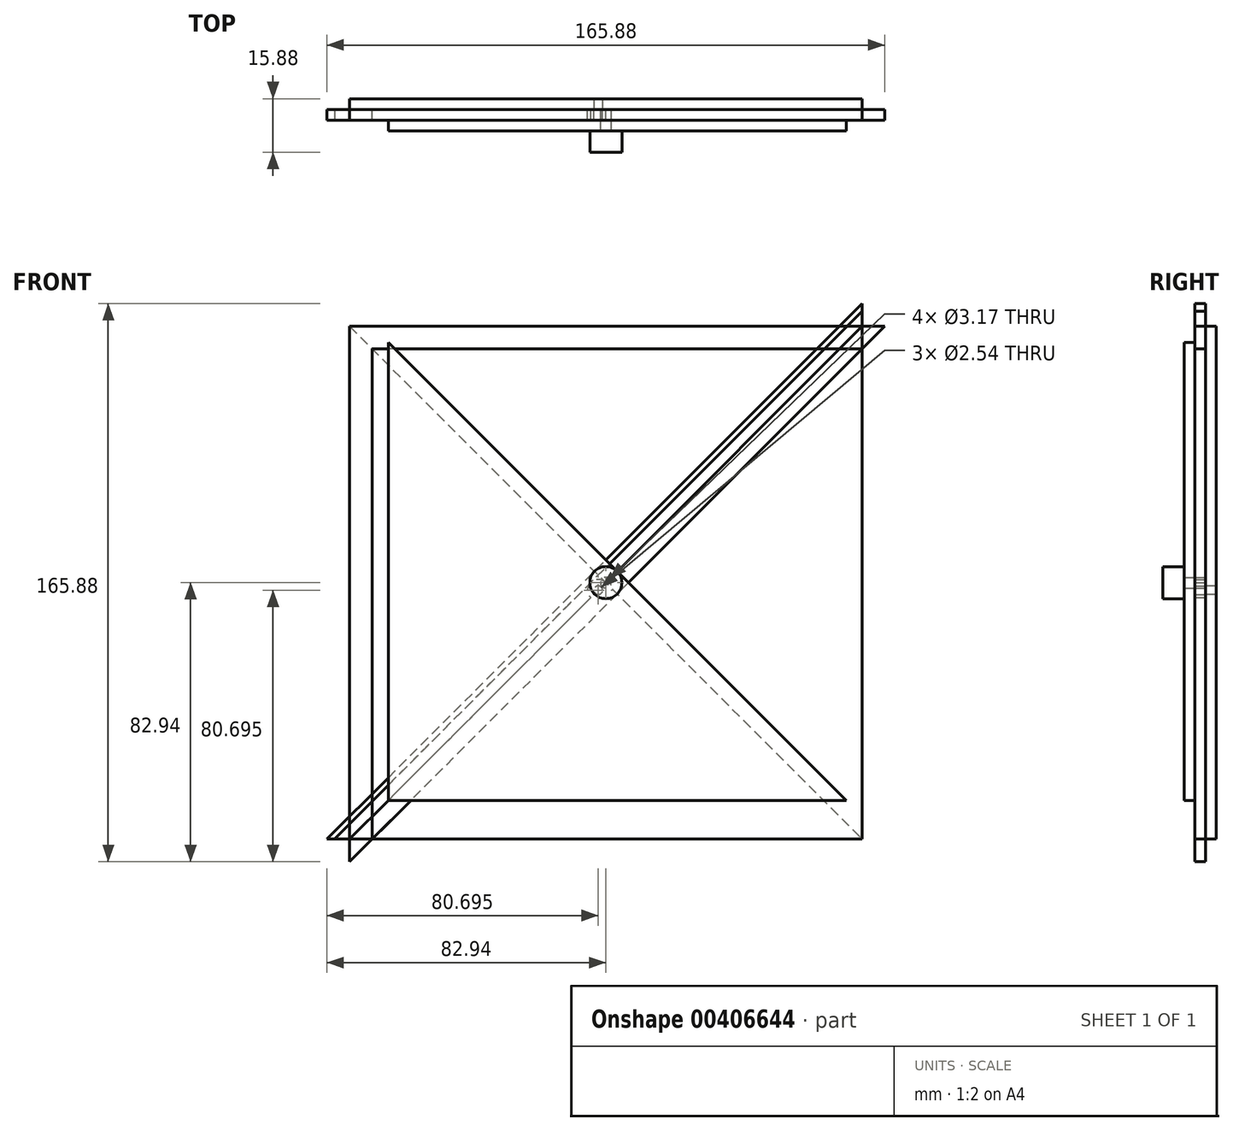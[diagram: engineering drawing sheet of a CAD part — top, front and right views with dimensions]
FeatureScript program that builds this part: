
annotation { "Feature Type Name" : "Feature", "Feature Type Description" : "" }
export const myFeature = defineFeature(function(context is Context, id is Id, definition is map)
    precondition{}
    {
        {
            var Q0;
            Q0=qCreatedBy(makeId("Front.planeOp"),FACE);
            var sketch = newSketch(context, id + "F0", { "sketchPlane" : qUnion([Q0])});
            skLineSegment(sketch, "E0.bottom", {"start": v(76.2, 76.2) * mm, "end": v(-76.2, 76.2) * mm});
            skLineSegment(sketch, "E0.top", {"start": v(76.2, -76.2) * mm, "end": v(-76.2, -76.2) * mm});
            skLineSegment(sketch, "E0.left", {"start": v(76.2, 76.2) * mm, "end": v(76.2, -76.2) * mm});
            skLineSegment(sketch, "E0.right", {"start": v(-76.2, 76.2) * mm, "end": v(-76.2, -76.2) * mm});
            skPoint(sketch, "E0.middle", {"position": v(0, 0) * mm});
            skLineSegment(sketch, "E1", {"start": v(-76.2, -76.2) * mm, "end": v(76.2, 76.2) * mm});
            skLineSegment(sketch, "E2", {"start": v(-76.2, 76.2) * mm, "end": v(76.2, -76.2) * mm});
            skCircle(sketch, "E3", {"center": v(-2.25, -2.25) * mm, "radius": 3.18 * mm});
            skSolve(sketch);
        }
        {
            var Q0;
            Q0=qCreatedBy(makeId("Front.planeOp"),FACE);
            var sketch = newSketch(context, id + "F1", { "sketchPlane" : qUnion([Q0])});
            skArc(sketch, "E4.0", {"start": v(0, 0) * mm, "mid": v(-4.5, 0) * mm, "end": v(-4.5, -4.5) * mm});
            skLineSegment(sketch, "E4.1", {"start": v(-76.2, -76.2) * mm, "end": v(-4.5, -4.5) * mm});
            skLineSegment(sketch, "E4.2", {"start": v(76.2, 76.2) * mm, "end": v(76.2, -76.2) * mm});
            skLineSegment(sketch, "E4.3", {"start": v(76.2, -76.2) * mm, "end": v(-76.2, -76.2) * mm});
            skLineSegment(sketch, "E5.trimOffspring", {"start": v(0, 0) * mm, "end": v(76.2, 76.2) * mm});
            skCircle(sketch, "E6", {"center": v(-2.25, -2.25) * mm, "radius": 1.27 * mm});
            skSolve(sketch);
        }
        {
            var Q0;
            Q0=qSketchRegion(id+"F1",true);
            extrude(context, id + "F2", {"entities" : qUnion([Q0]), "depth" : 3.17 * mm});
        }
        {
            var Q0;
            Q0=qCreatedBy(makeId("Front.planeOp"),FACE);
            var sketch = newSketch(context, id + "F3", { "sketchPlane" : qUnion([Q0])});
            skLineSegment(sketch, "E7.0", {"start": v(-76.2, 76.2) * mm, "end": v(76.2, -76.2) * mm});
            skLineSegment(sketch, "E7.1", {"start": v(-76.2, 76.2) * mm, "end": v(-76.2, -76.2) * mm});
            skLineSegment(sketch, "E7.2", {"start": v(76.2, -76.2) * mm, "end": v(-76.2, -76.2) * mm});
            skCircle(sketch, "E7.3", {"center": v(-2.25, -2.25) * mm, "radius": 1.27 * mm});
            skSolve(sketch);
        }
        {
            var Q0;
            Q0=qSketchRegion(id+"F3",true);
            extrude(context, id + "F4", {"entities" : qUnion([Q0]), "oppositeDirection" : true, "depth" : 3.17 * mm});
        }
        {
            var Q0;
            Q0=qCreatedBy(makeId("Right.planeOp"),FACE);
            var Q1;
            Q1=sQuery(id+"F0.wireOp",VERTEX,"E3.center");
            cPlane(context, id + "F5", {"entities" : qUnion([Q0, Q1]), "cplaneType" : CPlaneType.PLANE_POINT, "offset" : 25.4 * mm, "width" : 152.4 * mm, "height" : 152.4 * mm});
        }
        {
            var Q0;
            Q0=makeQuery(id+"F2.opExtrude","CAP_FACE",FACE,{"disambiguationData":[OSD([sQuery(id+"F1.wireOp",EDGE,"E4.0"),sQuery(id+"F1.wireOp",EDGE,"E4.1"),sQuery(id+"F1.wireOp",EDGE,"E4.2"),sQuery(id+"F1.wireOp",EDGE,"E4.3"),sQuery(id+"F1.wireOp",EDGE,"E5.trimOffspring"),sQuery(id+"F1.wireOp",EDGE,"E6")])],"isStart":false});
            var sketch = newSketch(context, id + "F6", { "sketchPlane" : qUnion([Q0])});
            skLineSegment(sketch, "E8", {"start": v(-4.5, 0) * mm, "end": v(76.2, 80.7) * mm});
            skLineSegment(sketch, "E9", {"start": v(-4.5, 0) * mm, "end": v(-80.7, -76.2) * mm});
            skLineSegment(sketch, "E10.0", {"start": v(76.2, -76.2) * mm, "end": v(-76.2, -76.2) * mm});
            skLineSegment(sketch, "E11.0", {"start": v(76.2, 76.2) * mm, "end": v(76.2, -76.2) * mm});
            skLineSegment(sketch, "E12", {"start": v(76.2, 76.2) * mm, "end": v(76.2, 80.7) * mm});
            skLineSegment(sketch, "E13", {"start": v(-76.2, -76.2) * mm, "end": v(-80.7, -76.2) * mm});
            skCircle(sketch, "E14.0", {"center": v(-2.25, -2.25) * mm, "radius": 1.27 * mm});
            skSolve(sketch);
        }
        {
            var Q0;
            Q0=qSketchRegion(id+"F6",true);
            extrude(context, id + "F7", {"entities" : qUnion([Q0]), "oppositeDirection" : true, "depth" : 3.17 * mm});
        }
        {
            var Q0;
            Q0=qCreatedBy(makeId("Front.planeOp"),FACE);
            var sketch = newSketch(context, id + "F8", { "sketchPlane" : qUnion([Q0])});
            skCircle(sketch, "E15", {"center": v(0, 0) * mm, "radius": 1.59 * mm});
            skCircle(sketch, "E16", {"center": v(0, 0) * mm, "radius": 4.76 * mm, "construction": true});
            skLineSegment(sketch, "E17.0", {"start": v(76.2, 76.2) * mm, "end": v(76.2, -76.2) * mm});
            skLineSegment(sketch, "E17.1", {"start": v(76.2, -76.2) * mm, "end": v(-76.2, -76.2) * mm});
            skLineSegment(sketch, "E18.0", {"start": v(-76.2, -76.2) * mm, "end": v(76.2, 76.2) * mm, "construction": true});
            skLineSegment(sketch, "E19", {"start": v(-3.37, 3.37) * mm, "end": v(76.2, 82.94) * mm});
            skLineSegment(sketch, "E20.0", {"start": v(-76.2, 76.2) * mm, "end": v(76.2, -76.2) * mm, "construction": true});
            skLineSegment(sketch, "E21", {"start": v(76.2, 76.2) * mm, "end": v(76.2, 82.94) * mm});
            skLineSegment(sketch, "E22", {"start": v(-3.37, 3.37) * mm, "end": v(-82.94, -76.2) * mm});
            skLineSegment(sketch, "E23", {"start": v(-76.2, -76.2) * mm, "end": v(-82.94, -76.2) * mm});
            skSolve(sketch);
        }
        {
            var Q0;
            Q0=qSketchRegion(id+"F8",true);
            var Q1;
            Q1=qConstructionFilter(qBodyType(qCreatedBy(id+"F8",EDGE),BodyType.WIRE),ConstructionObject.NO);
            extrude(context, id + "F9", {"entities" : qUnion([Q0]), "surfaceEntities" : qUnion([Q1]), "depth" : 3.17 * mm});
        }
        {
            var Q0;
            Q0=qCreatedBy(makeId("Right.planeOp"),FACE);
            var sketch = newSketch(context, id + "F10", { "sketchPlane" : qUnion([Q0])});
            skLineSegment(sketch, "E24.0", {"start": v(-3.18, -1.59) * mm, "end": v(-3.18, 1.59) * mm, "construction": true});
            skLineSegment(sketch, "E25", {"start": v(-3.17, 0) * mm, "end": v(-130.06, 0) * mm, "construction": true});
            skSolve(sketch);
        }
        {
            var Q0;
            Q0=makeQuery(id+"F9.opExtrude","SWEPT_BODY",BODY,{"disambiguationData":[OSD([sQuery(id+"F8.wireOp",EDGE,"E15"),sQuery(id+"F8.wireOp",EDGE,"E17.0"),sQuery(id+"F8.wireOp",EDGE,"E17.1"),sQuery(id+"F8.wireOp",EDGE,"E19"),sQuery(id+"F8.wireOp",EDGE,"E21"),sQuery(id+"F8.wireOp",EDGE,"E22"),sQuery(id+"F8.wireOp",EDGE,"E23")])]});
            var Q1;
            Q1=sQuery(id+"F10.wireOp",EDGE,"E25");
            transform(context, id + "F11", {"entities" : qUnion([Q0]), "transformType" : TransformType.ROTATION, "transformAxis" : qUnion([Q1]), "angle" : 180 * degree, "makeCopy" : true});
        }
        {
            var Q0;
            Q0=qCreatedBy(makeId("Front.planeOp"),FACE);
            var sketch = newSketch(context, id + "F12", { "sketchPlane" : qUnion([Q0])});
            skLineSegment(sketch, "E26.0", {"start": v(76.2, 76.2) * mm, "end": v(-76.2, 76.2) * mm, "construction": true});
            skLineSegment(sketch, "E26.1", {"start": v(-76.2, 76.2) * mm, "end": v(-76.2, -76.2) * mm, "construction": true});
            skLineSegment(sketch, "E26.2", {"start": v(76.2, 69.46) * mm, "end": v(-69.46, -76.2) * mm});
            skLineSegment(sketch, "E26.3", {"start": v(76.2, 76.2) * mm, "end": v(76.2, -76.2) * mm, "construction": true});
            skLineSegment(sketch, "E26.4", {"start": v(76.2, -76.2) * mm, "end": v(-76.2, -76.2) * mm, "construction": true});
            skCircle(sketch, "E26.5", {"center": v(0, 0) * mm, "radius": 1.59 * mm});
            skLineSegment(sketch, "E27", {"start": v(-69.46, -76.2) * mm, "end": v(-69.46, 69.46) * mm});
            skLineSegment(sketch, "E28", {"start": v(76.2, 69.46) * mm, "end": v(-69.46, 69.46) * mm});
            skPoint(sketch, "E29.orphan", {"position": v(82.94, 76.2) * mm});
            skPoint(sketch, "E30.orphan", {"position": v(-76.2, -82.94) * mm});
            skSolve(sketch);
        }
        {
            var Q0;
            Q0=qSketchRegion(id+"F12",true);
            extrude(context, id + "F13", {"entities" : qUnion([Q0]), "depth" : 3.17 * mm});
        }
        {
            var Q0;
            Q0=makeQuery(id+"F13.opExtrude","CAP_FACE",FACE,{"disambiguationData":[OSD([sQuery(id+"F12.wireOp",EDGE,"E26.2"),sQuery(id+"F12.wireOp",EDGE,"E26.5"),sQuery(id+"F12.wireOp",EDGE,"E27"),sQuery(id+"F12.wireOp",EDGE,"E28")])],"isStart":false});
            var sketch = newSketch(context, id + "F14", { "sketchPlane" : qUnion([Q0])});
            skCircle(sketch, "E31.0", {"center": v(0, 0) * mm, "radius": 1.59 * mm});
            skLineSegment(sketch, "E32.0", {"start": v(71.44, 64.7) * mm, "end": v(-64.7, -71.44) * mm});
            skLineSegment(sketch, "E33.0", {"start": v(71.44, 64.7) * mm, "end": v(-64.7, 64.7) * mm});
            skLineSegment(sketch, "E34.0", {"start": v(-64.7, -71.44) * mm, "end": v(-64.7, 64.7) * mm});
            skPoint(sketch, "E35.orphan", {"position": v(-69.46, -76.2) * mm});
            skPoint(sketch, "E36.orphan", {"position": v(76.2, 69.46) * mm});
            skSolve(sketch);
        }
        {
            var Q0;
            Q0=qSketchRegion(id+"F14",true);
            extrude(context, id + "F15", {"entities" : qUnion([Q0]), "depth" : 3.17 * mm});
        }
        {
            var Q0;
            Q0=qCreatedBy(makeId("Top.planeOp"),FACE);
            var sketch = newSketch(context, id + "F16", { "sketchPlane" : qUnion([Q0])});
            skLineSegment(sketch, "E37.0", {"start": v(1.59, -6.35) * mm, "end": v(-1.59, -6.35) * mm, "construction": true});
            skLineSegment(sketch, "E38", {"start": v(0, -6.35) * mm, "end": v(0, -31.16) * mm});
            skSolve(sketch);
        }
        {
            var Q0;
            Q0=makeQuery(id+"F15.opExtrude","SWEPT_BODY",BODY,{"disambiguationData":[OSD([sQuery(id+"F14.wireOp",EDGE,"E31.0"),sQuery(id+"F14.wireOp",EDGE,"E32.0"),sQuery(id+"F14.wireOp",EDGE,"E33.0"),sQuery(id+"F14.wireOp",EDGE,"E34.0")])]});
            var Q1;
            Q1=sQuery(id+"F16.wireOp",EDGE,"E38");
            transform(context, id + "F17", {"entities" : qUnion([Q0]), "transformType" : TransformType.ROTATION, "transformAxis" : qUnion([Q1]), "angle" : 90 * degree, "makeCopy" : false});
        }
        {
            var Q0;
            Q0=makeQuery(id+"F15.opExtrude","CAP_FACE",FACE,{"disambiguationData":[OSD([sQuery(id+"F14.wireOp",EDGE,"E31.0"),sQuery(id+"F14.wireOp",EDGE,"E32.0"),sQuery(id+"F14.wireOp",EDGE,"E33.0"),sQuery(id+"F14.wireOp",EDGE,"E34.0")])],"isStart":false});
            var sketch = newSketch(context, id + "F18", { "sketchPlane" : qUnion([Q0])});
            skCircle(sketch, "E39.0", {"center": v(0, 0) * mm, "radius": 1.59 * mm, "construction": true});
            skCircle(sketch, "E40", {"center": v(0, 0) * mm, "radius": 4.76 * mm});
            skSolve(sketch);
        }
        {
            var Q0;
            Q0=qSketchRegion(id+"F18",true);
            var Q1;
            Q1=sQuery(id+"F18.wireOp",EDGE,"E39.0");
            extrude(context, id + "F19", {"entities" : qUnion([Q0]), "surfaceEntities" : qUnion([Q1]), "depth" : 6.35 * mm});
        }
    });
